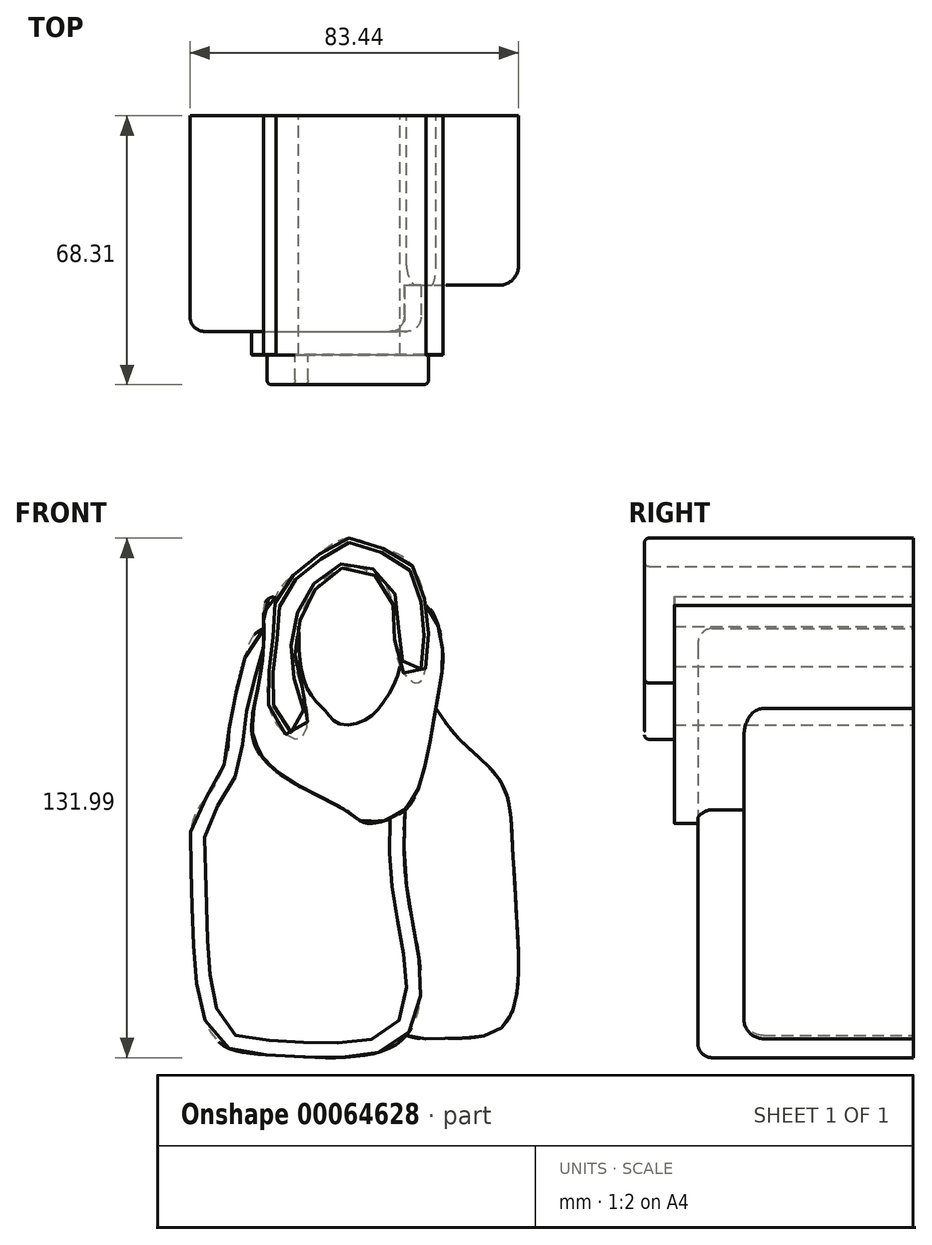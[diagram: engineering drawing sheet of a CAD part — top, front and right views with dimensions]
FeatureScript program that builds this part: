
annotation { "Feature Type Name" : "Feature", "Feature Type Description" : "" }
export const myFeature = defineFeature(function(context is Context, id is Id, definition is map)
    precondition{}
    {
        {
            var Q0;
            Q0=qCreatedBy(makeId("Front.planeOp"),FACE);
            var sketch = newSketch(context, id + "F0", { "sketchPlane" : qUnion([Q0])});
            skFitSpline(sketch, "E0", {"points": [v(0, 59.31) * mm, v(-5.1, 57.15) * mm, v(-11.26, 52.06) * mm, v(-17.51, 46.76) * mm, v(-18.84, 42.03) * mm, v(-19.93, 27.8) * mm, v(-20.67, 23.87) * mm, v(-19.2, 13.29) * mm, v(-12.55, 8.37) * mm, v(-10.58, 16.49) * mm, v(-13.35, 25.75) * mm, v(-12.02, 39.94) * mm, v(-5.77, 49.4) * mm, v(0, 52.08) * mm, v(5.2, 50.73) * mm, v(10.7, 44.3) * mm, v(12.55, 27.56) * mm, v(17.72, 22.64) * mm, v(19.93, 30.76) * mm, v(19.97, 38.43) * mm, v(15.62, 52.82) * mm, v(6.53, 57.36) * mm, v(0, 59.31) * mm]});
            skSolve(sketch);
        }
        {
            var Q0;
            Q0=qCreatedBy(makeId("Front.planeOp"),FACE);
            var sketch = newSketch(context, id + "F1", { "sketchPlane" : qUnion([Q0])});
            skFitSpline(sketch, "E1", {"points": [v(-12.8, 34.2) * mm, v(-15.05, 43.35) * mm, v(-20.67, 43.8) * mm, v(-21.68, 37.67) * mm, v(-22.81, 23.1) * mm, v(-24.51, 8.7) * mm, v(-16, -1.7) * mm, v(0, -10.41) * mm, v(4.26, -13.06) * mm, v(12.78, -10.8) * mm, v(17.89, -3.4) * mm, v(22.64, 19.44) * mm, v(23.63, 32.24) * mm, v(19.2, 42.33) * mm, v(14.48, 39.75) * mm, v(13.54, 37.3) * mm, v(13.54, 33.13) * mm, v(12.59, 25.37) * mm, v(8.61, 17.42) * mm, v(3.5, 12.87) * mm, v(-2.93, 12.3) * mm, v(-5.96, 15.33) * mm, v(-8.61, 17.98) * mm, v(-11.64, 23.66) * mm, v(-12.8, 34.2) * mm]});
            skSolve(sketch);
        }
        {
            var Q0;
            Q0=qCreatedBy(makeId("Front.planeOp"),FACE);
            var sketch = newSketch(context, id + "F2", { "sketchPlane" : qUnion([Q0])});
            skFitSpline(sketch, "E2", {"points": [v(-16, 31.75) * mm, v(-18.46, 36.54) * mm, v(-23.63, 35.2) * mm, v(-26.58, 28.55) * mm, v(-30.38, 11.74) * mm, v(-31.14, 3.79) * mm, v(-34.74, -4.35) * mm, v(-39.47, -11.74) * mm, v(-40.04, -29.34) * mm, v(-34.93, -66.63) * mm, v(-18.46, -72.12) * mm, v(11.45, -69.66) * mm, v(18.27, -54.14) * mm, v(14.67, -29.72) * mm, v(14.86, -3.98) * mm, v(14.67, 9.28) * mm, v(4.26, 10.22) * mm, v(-4.64, 9.84) * mm, v(-8.23, 11.93) * mm, v(-15.62, 22.34) * mm, v(-16, 31.75) * mm]});
            skSolve(sketch);
        }
        {
            var Q0;
            Q0=qCreatedBy(makeId("Front.planeOp"),FACE);
            var sketch = newSketch(context, id + "F3", { "sketchPlane" : qUnion([Q0])});
            skFitSpline(sketch, "E3", {"points": [v(10.32, 18.17) * mm, v(17.51, 20.82) * mm, v(23.57, 13.82) * mm, v(29.44, 6.81) * mm, v(38.71, -2.84) * mm, v(41.36, -15.9) * mm, v(42.69, -39.56) * mm, v(39.28, -64.55) * mm, v(23.95, -67.77) * mm, v(13.16, -66.26) * mm, v(0, -36.72) * mm, v(10.32, 18.17) * mm]});
            skSolve(sketch);
        }
        {
            var Q0;
            Q0 = qSketchRegion(id + "F0", true);
            extrude(context, id + "F4", {"entities" : qUnion([Q0]), "depth" : 68.3 * mm});
        }
        {
            var Q0;
            Q0 = qSketchRegion(id + "F1", true);
            extrude(context, id + "F5", {"entities" : qUnion([Q0]), "operationType" : NewBodyOperationType.ADD, "depth" : 60.73 * mm});
        }
        {
            var Q0;
            Q0 = qSketchRegion(id + "F2", true);
            extrude(context, id + "F6", {"entities" : qUnion([Q0]), "operationType" : NewBodyOperationType.ADD, "depth" : 54.78 * mm});
        }
        {
            var Q0;
            Q0 = qSketchRegion(id + "F3", true);
            extrude(context, id + "F7", {"entities" : qUnion([Q0]), "operationType" : NewBodyOperationType.ADD, "depth" : 43.05 * mm});
        }
        {
            var Q0;
            Q0=makeQuery(id+"F7.opExtrude","CAP_EDGE",EDGE,{"disambiguationData":[OSD([sQuery(id+"F3.wireOp",EDGE,"E3")])],"isStart":false});
            fillet(context, id + "F8", {"entities" : qUnion([Q0]), "radius" : 5 * mm, "tangentPropagation" : true, "allowEdgeOverflow" : false});
        }
        {
            var Q0;
            Q0=makeQuery(id+"F5.boolean.opBoolean","SPLIT",EDGE,{"disambiguationData":[OD(0.0)],"derivedFrom":makeQuery(id+"F5.opExtrude","CAP_EDGE",EDGE,{"disambiguationData":[OSD([sQuery(id+"F1.wireOp",EDGE,"E1")])],"isStart":false})});
            fillet(context, id + "F9", {"entities" : qUnion([Q0]), "radius" : 0.02 * mm, "tangentPropagation" : true, "allowEdgeOverflow" : false});
        }
        {
            var Q0;
            Q0=makeQuery(id+"F6.opExtrude","CAP_EDGE",EDGE,{"disambiguationData":[OSD([sQuery(id+"F2.wireOp",EDGE,"E2")])],"isStart":false});
            fillet(context, id + "F10", {"entities" : qUnion([Q0]), "radius" : 3.67 * mm, "tangentPropagation" : true, "allowEdgeOverflow" : false});
        }
        {
            var Q0;
            Q0=makeQuery(id+"F4.opExtrude","CAP_EDGE",EDGE,{"disambiguationData":[OSD([sQuery(id+"F0.wireOp",EDGE,"E0")])],"isStart":false});
            fillet(context, id + "F11", {"entities" : qUnion([Q0]), "radius" : 1.13 * mm, "tangentPropagation" : true, "allowEdgeOverflow" : false});
        }
    });
